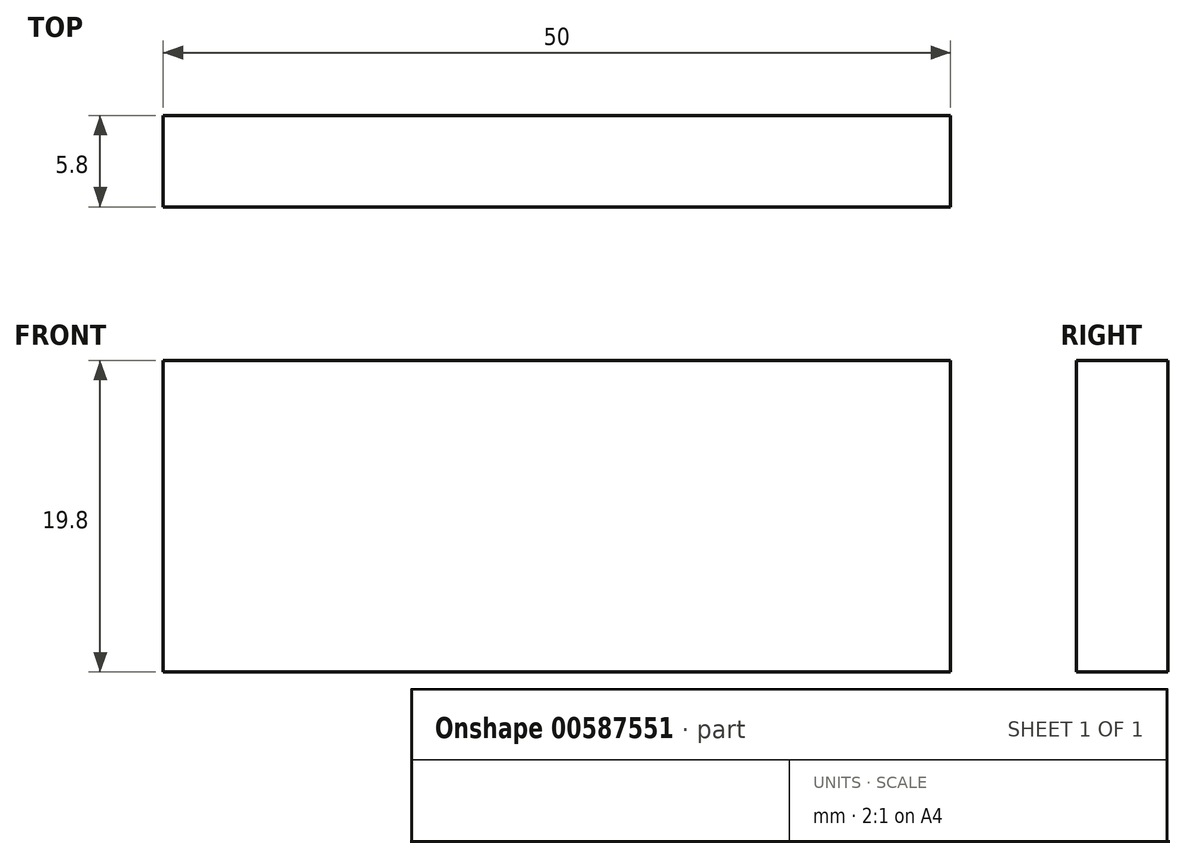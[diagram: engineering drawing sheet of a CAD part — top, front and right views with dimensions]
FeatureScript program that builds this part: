
annotation { "Feature Type Name" : "Feature", "Feature Type Description" : "" }
export const myFeature = defineFeature(function(context is Context, id is Id, definition is map)
    precondition{}
    {
        {
            var Q0;
            Q0=qCreatedBy(makeId("Front.planeOp"),FACE);
            var sketch = newSketch(context, id + "F0", { "sketchPlane" : qUnion([Q0])});
            skLineSegment(sketch, "E0.bottom", {"start": v(-60.67, 30.56) * mm, "end": v(-10.67, 30.56) * mm});
            skLineSegment(sketch, "E0.top", {"start": v(-60.67, 10.76) * mm, "end": v(-10.67, 10.76) * mm});
            skLineSegment(sketch, "E0.left", {"start": v(-60.67, 30.56) * mm, "end": v(-60.67, 10.76) * mm});
            skLineSegment(sketch, "E0.right", {"start": v(-10.67, 30.56) * mm, "end": v(-10.67, 10.76) * mm});
            skSolve(sketch);
        }
        {
            var Q0;
            Q0 = qSketchRegion(id + "F0", true);
            extrude(context, id + "F1", {"entities" : qUnion([Q0]), "depth" : 5.8 * mm, "offsetDistance" : 25 * mm});
        }
    });
